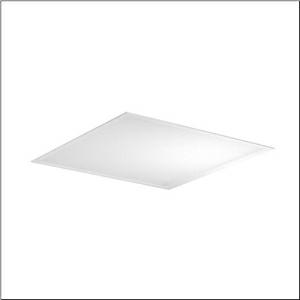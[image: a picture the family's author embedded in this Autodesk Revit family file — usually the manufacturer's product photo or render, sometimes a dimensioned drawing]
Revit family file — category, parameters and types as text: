
# Revit family: apollon_21_square_51mq12wd2t13
name_source: partatom
category: Lighting Fixtures
units: mm (PartAtom-declared; Revit-internal decimal feet)

## family parameters
Cut with Voids When Loaded = No
Host = Face
Light Source = No
Part Type = Normal
Room Calculation Point = No
Round Connector Dimension = Use Diameter
Shared = No

## types (1)
- --- (1 x LED 2700 K ... 6500 K, 4000 lm, 40 W, 2700K)
    Apparent Load = 40 VA
    CIE Flux Codes = 61 87 97 100 100
    Color Rendering = 80
    Color Temperature = 2700K
    Default Elevation = 1800 mm
    Description = Apollon 21 square, office luminaire, primary optical cover: micro prismatic cover, of PMMA, CAT 2 (L<= 3000cd/m²), light emission: direct distribution, primary light characteristic: symmetric, installation type: lay-in mounting, LED, rated luminous flux: 4.000lm, luminous efficacy: 100lm/W, light colour: 8tw, colour temperature: 2700..6500K, control gear: DALI-2 DT8, with terminal, 5-pole, mains connection: 220..240V, AC, 50/60Hz, rated input power: 40W, housing, of aluminium, traffic white (RAL 9016), module: M600, length: 596mm, width: 596mm, height: 40mm, housing upper side, of sheet steel, galvanised, protection rating (complete): IP20, protection rating (lamp compartment, on room side): IP50, insulation class (complete): insulation class I (protective earthing), certification: CE, ENEC, permissible operating ambient temperature: -20..+40°C, packaging unit: 1 piece
    Height = 0 mm  [stored 0 ft]
    Lamp = 1 x LED 2700 K ... 6500 K
    Lamp Light Flux = 4000 lm
    Lamp Power = 40 W
    Lamp count = 1
    Length = 595 mm
    Luminous efficacy = 100 lm/W
    Manufacturer = Siteco
    ModVariant = No
    Model = 51MQ12WD2T13
    Mounting Place = Ceiling
    Mounting Type = Recessed
    Number of Poles = 1
    OnlyDefault = Yes
    Power Factor = 1
    Product Name = Apollon 21 square
    Product group = office luminaire | ceiling recessed
    ProductGroupID = 400
    Protection Class = Protection class I
    Protection Degree = IP 20
    RLX_Detail_Level = 1
    RLX_Emergency_Light_Flux = 0 lm
    RLX_Emergency_Type = 0
    RLX_Emergency_Type_DB = No
    RlxData = <blob elided: 12633 chars, md5=8689edc7>
    Socket = socket
    Standby Power = 0 W
    System Light Flux = 4000 lm
    System Power = 40 W
    Type Comments = individual setting: CCT=2700K
    Type Image = l_1291049.jpg
    URL = http://relux.com
    VarID = @adj_123751
    Voltage = 0 V
    Weight = 0.00 kg
    Width = 595 mm

note: [stored X ft] marks values corroborated as IEEE doubles in the binary element streams (Revit-internal decimal feet)

## geometry (parser evidence)
native form markers: Sweep x11
no freeform markers — native parametric forms only
